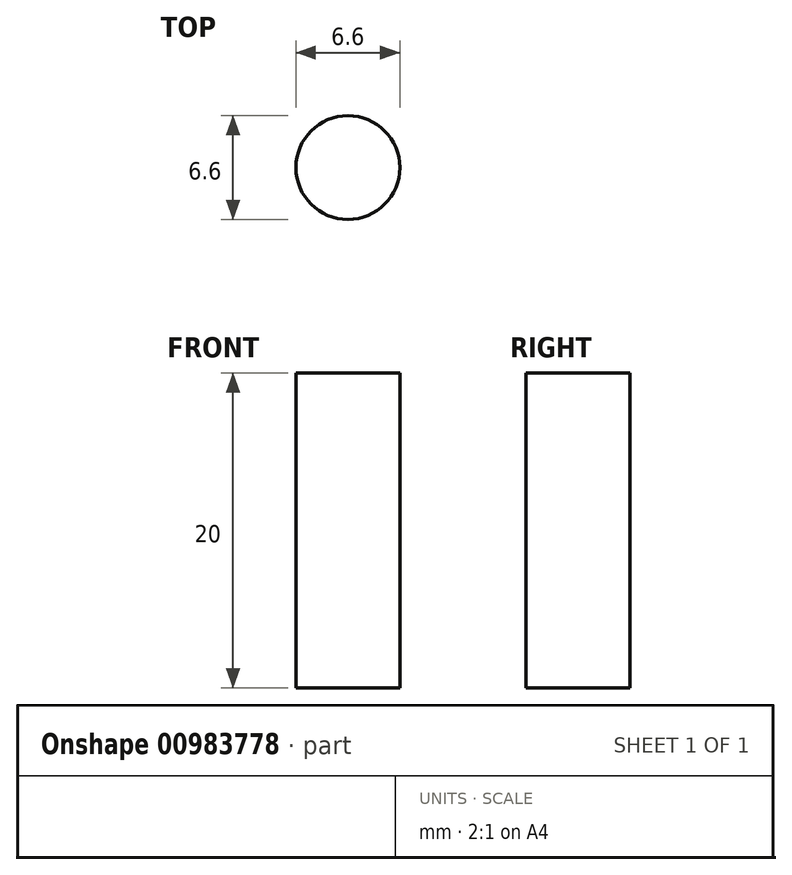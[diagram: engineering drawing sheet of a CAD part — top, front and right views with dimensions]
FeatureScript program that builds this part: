
annotation { "Feature Type Name" : "Feature", "Feature Type Description" : "" }
export const myFeature = defineFeature(function(context is Context, id is Id, definition is map)
    precondition{}
    {
        {
            var Q0;
            Q0=qCreatedBy(makeId("Top.planeOp"),FACE);
            var sketch = newSketch(context, id + "F0", { "sketchPlane" : qUnion([Q0])});
            skCircle(sketch, "E0", {"center": v(0, 0) * mm, "radius": 3.3 * mm});
            skSolve(sketch);
        }
        {
            var Q0;
            Q0 = qSketchRegion(id + "F0", true);
            extrude(context, id + "F1", {"entities" : qUnion([Q0]), "depth" : 20 * mm, "offsetDistance" : 25 * mm});
        }
    });
